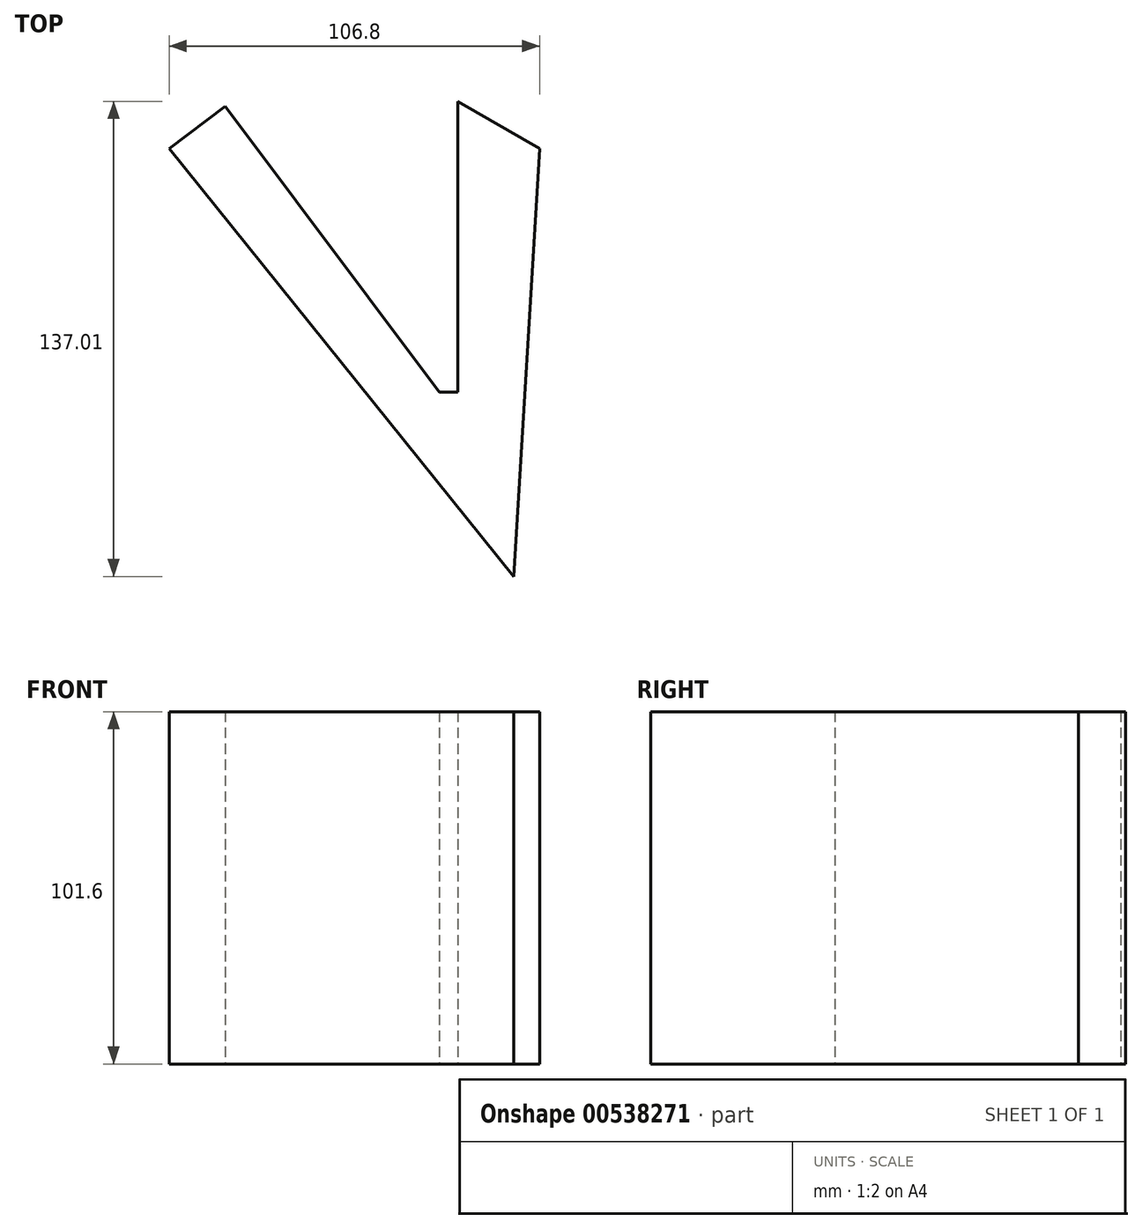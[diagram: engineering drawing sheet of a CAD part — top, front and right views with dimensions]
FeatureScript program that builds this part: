
annotation { "Feature Type Name" : "Feature", "Feature Type Description" : "" }
export const myFeature = defineFeature(function(context is Context, id is Id, definition is map)
    precondition{}
    {
        {
            var Q0;
            Q0=qCreatedBy(makeId("Top.planeOp"),FACE);
            var sketch = newSketch(context, id + "F0", { "sketchPlane" : qUnion([Q0])});
            skLineSegment(sketch, "E0", {"start": v(-46.73, 44.03) * mm, "end": v(15.02, -38.3) * mm});
            skLineSegment(sketch, "E1", {"start": v(20.38, -38.3) * mm, "end": v(20.38, 45.52) * mm});
            skLineSegment(sketch, "E2", {"start": v(-46.73, 44.03) * mm, "end": v(-62.87, 31.93) * mm});
            skLineSegment(sketch, "E3", {"start": v(-62.87, 31.93) * mm, "end": v(36.43, -91.49) * mm});
            skLineSegment(sketch, "E4", {"start": v(20.38, 45.52) * mm, "end": v(43.93, 31.93) * mm});
            skLineSegment(sketch, "E5", {"start": v(43.93, 31.93) * mm, "end": v(36.43, -91.49) * mm});
            skLineSegment(sketch, "E6", {"start": v(20.38, -38.3) * mm, "end": v(15.02, -38.3) * mm});
            skSolve(sketch);
        }
        {
            var Q0;
            Q0 = qSketchRegion(id + "F0", true);
            extrude(context, id + "F1", {"entities" : qUnion([Q0]), "depth" : 101.6 * mm, "offsetDistance" : 25.4 * mm});
        }
    });
